# Revit family: BC_Hitachi_RAS-4-6H(V)RP2E_LOD400
name_source: partatom
category: Equipement de génie climatique
revit_build: Autodesk Revit 2018 (Build: 20181015_0930(x64)
units: mm (PartAtom-declared; Revit-internal decimal feet)

## family parameters
Basée sur le plan de construction = Non
Cote de connecteur circulaire = Utiliser le diamètre
Couper avec des vides une fois chargée = Non
Numéro OmniClass = 23.75.00.00
Partagée = Non
Point de calcul de pièce = Non
Titre OmniClass = Climate Control (HVAC)
Toujours verticalement = Oui
Type d'élément = Normal

## types (6) — shared parameters
BC_OBJECT_ID = 215290
BC_OBJECT_VERSION = #7
Compressor Type = Rotative DC Inverter driven
Description = IVX Prime R32
Frequency = 50 Hz
Gas Diameter = 15.88 mm
Heating Capacity Min = 5 kW
Height difference between OU & IU (higher OU) = 30000.00 mm
Height difference between OU & IU (lower OU) = 20000.00 mm
Liquid Diameter = 9.52 mm
Manufacturer = Hitachi Air Conditioning Europe SAS
MasterFormat = Split-System Air-Conditioners
Masterformat Code = 23 81 26
Material = IVX Material
Maximum chargless piping length = 20000.00 mm
Maximum connectable indoor units = 4
Maximum connected capacity = 115 %
Maximum piping length (additional refrigerant needed) = 75
Miminum piping length = 5000.00 mm
Minimum connectable indoor units = 1
Minimum connected capacity = 90 %
Modèle = IVX Prime R32
Name BIM&CO = Outdoor Unit
Nominal Air Flow = 4800.0 m³/h
OMNICLASS Table 23 Code  = 23.75.00.00
Omniclass = Climate Control (HVAC)
Overall Depth = 370.00 mm
Overall Height = 1140.00 mm
Overall Width = 950.00 mm
Recommended circuit breaker = 20 A
Refrigerant Type = R32
Refrigerant charge before shipment = 3.00 kg
Size of power cable (according to EN 60335-1) = 5 x 4.0 mm²
Size of transmission cable between indoor unit and outdoor unit = 2 x 0.75 mm²
Sound level = 69
Sound pressure level Night mode cooling (dB(A)) = 50
Starting current (A) = Less than maximum current
Uniformat = Distribution Systems
Uniformat code = D3040
Wired Remote control model (Optional) = PC-ARFPE

## per-type parameters (varying)
| type | BC_VARIANT_ID | Coefficient of Performance (COP) | Commentaires du type | Cooling Capacity | Cooling Capacity Max | Cooling Capacity Min | Cooling Running Current | Cooling Sound Pressure Level | Energy efficiency ratio (EER) | Heating Capacity | Heating Capacity Max | Heating Running Current | Heating Sound Pressure Level | Maximum Current | Net Weight | Nominal Voltage | Number of Poles | Sound Level |
| RAS-6HVRP2E | 561991 | 4.4 | Outdoor unit - RAS-6HVRP2E | 14 kW | 18 kW | 5 kW | 21 A | 56 | 3.24 | 16 kW | 22 kW | 18 A | 56 | 23 A | 84.00 kg | 400 V | 3 | 72 |
| RAS-5HVRP2E | 561989 | 4.13 | Outdoor unit - RAS-5HVRP2E | 13 kW | 16 kW | 6 kW | 17 A | 56 | 3.66 | 14 kW | 19 kW | 16 A | 56 | 23 A | 84.00 kg | 230 V | 1 | 72 |
| RAS-6HRP2E | 561992 | 4.4 | Outdoor unit - RAS-6HRP2E | 14 kW | 18 kW | 6 kW | 7 A | 56 | 3.24 | 16 kW | 22 kW | 6 A | 56 | 15 A | 86.00 kg | 400 V | 3 | 72 |
| RAS-5HRP2E | 561990 | 4.13 | Outdoor unit - RAS-5HRP2E | 13 kW | 16 kW | 6 kW | 6 A | 56 | 3.66 | 14 kW | 19 kW | 6 A | 56 | 15 A | 86.00 kg | 400 V | 3 | 72 |
| RAS-4HVRP2E | 561987 | 4.31 | Outdoor unit - RAS-4HVRP2E | 10 kW | 13 kW | 5 kW | 12 A | 54 | 3.98 | 11 kW | 17 kW | 13 A | 54 | 23 A | 84.00 kg | 230 V | 1 | 70 |
| RAS-4HRP2E | 561988 | 4.31 | Outdoor unit - RAS-4HRP2E | 10 kW | 13 kW | 6 kW | 4 A | 54 | 3.98 | 11 kW | 17 kW | 4 A | 54 | 15 A | 86.00 kg | 230 V | 1 | 70 |

note: column(s) folded — value = type name in every type: Product Code, Reference
